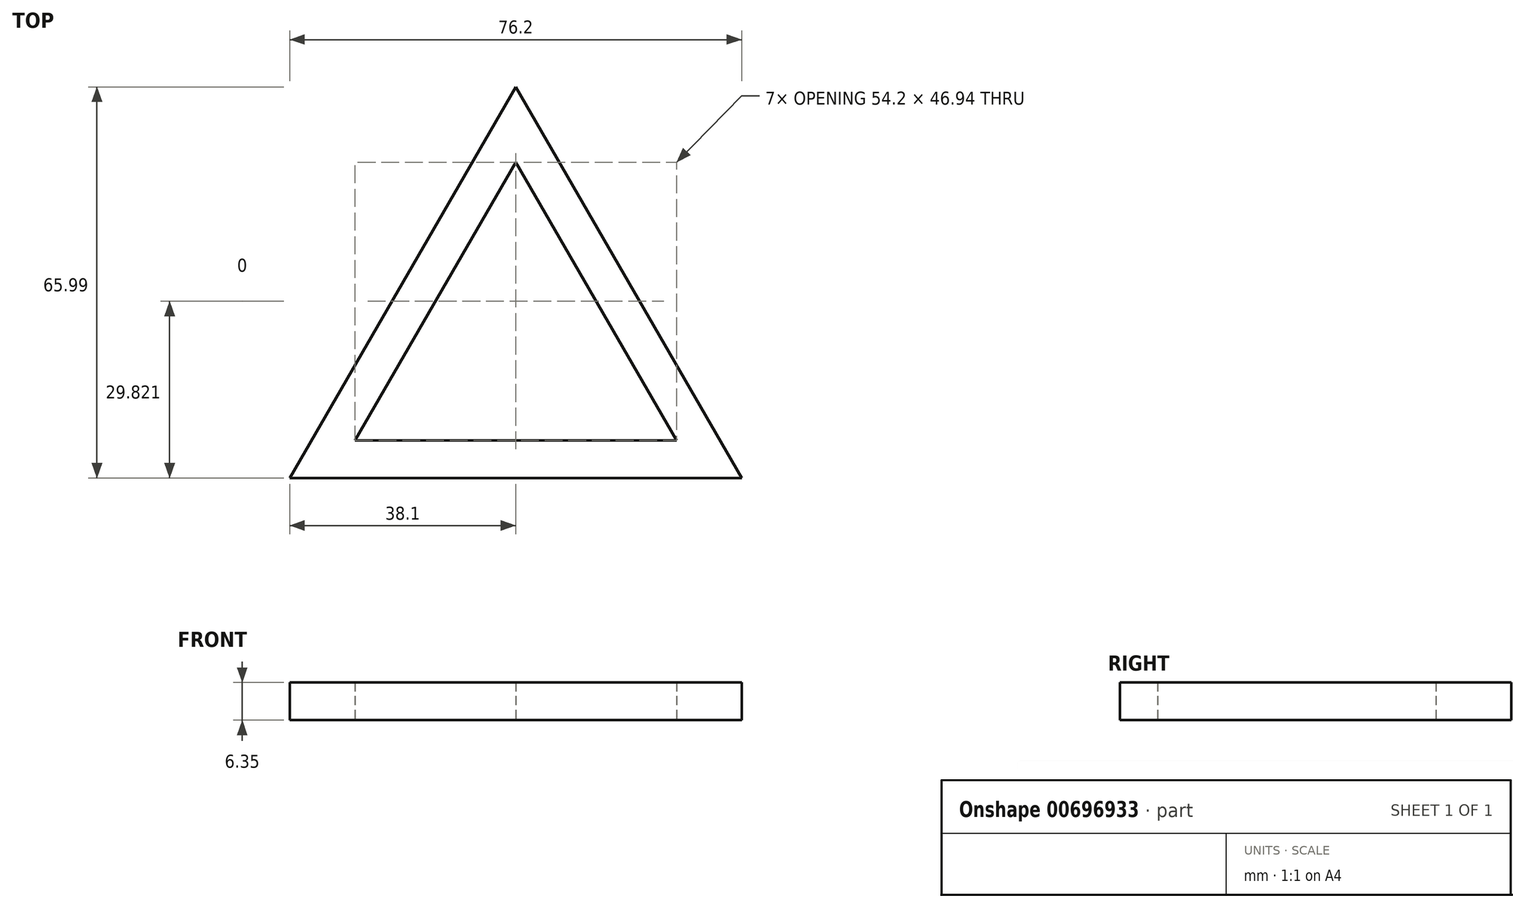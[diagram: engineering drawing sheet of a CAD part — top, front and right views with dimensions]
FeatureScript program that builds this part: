
annotation { "Feature Type Name" : "Feature", "Feature Type Description" : "" }
export const myFeature = defineFeature(function(context is Context, id is Id, definition is map)
    precondition{}
    {
        {
            var Q0;
            Q0=qCreatedBy(makeId("Top.planeOp"),FACE);
            var sketch = newSketch(context, id + "F0", { "sketchPlane" : qUnion([Q0])});
            skLineSegment(sketch, "E0", {"start": v(-38.1, 0) * mm, "end": v(38.1, 0) * mm});
            skLineSegment(sketch, "E1", {"start": v(38.1, 0) * mm, "end": v(0, 66) * mm});
            skLineSegment(sketch, "E2", {"start": v(0, 66) * mm, "end": v(-38.1, 0) * mm});
            skLineSegment(sketch, "E3.0", {"start": v(0, 53.3) * mm, "end": v(-27.1, 6.35) * mm});
            skLineSegment(sketch, "E3.1", {"start": v(27.1, 6.35) * mm, "end": v(0, 53.3) * mm});
            skLineSegment(sketch, "E3.2", {"start": v(-27.1, 6.35) * mm, "end": v(27.1, 6.35) * mm});
            skSolve(sketch);
        }
        {
            var Q0;
            Q0=makeQuery(id+"F0.imprint","IMPRINT",FACE,{"disambiguationData":[TD([[makeQuery(id+"F0.imprint","IMPRINT",EDGE,{"derivedFrom":sQuery(id+"F0.wireOp",EDGE,"E0")}),1.0]])]});
            extrude(context, id + "F1", {"entities" : qUnion([Q0]), "depth" : 6.35 * mm, "offsetDistance" : 25.4 * mm});
        }
    });
